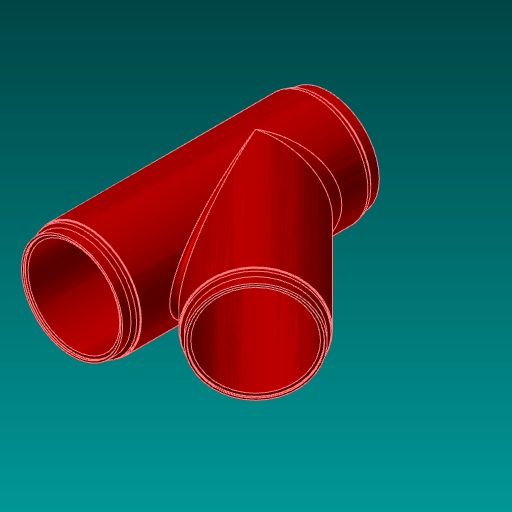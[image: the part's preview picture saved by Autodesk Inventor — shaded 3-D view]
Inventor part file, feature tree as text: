
AUTODESK INVENTOR PART (.ipt)
format: ipt  version: 2017.3 (Build 213256000, 256)  size: 343,040 bytes
history: native  units: in
note: dims shown in document units (in); Inventor stores cm internally (conversion verified against a paired STEP export)
features: extrude x12, sketch x8, fillet x6, chamfer x2, plane x1
ambient origin geometry x8: Origin, YZ Plane, XZ Plane, XY Plane, X Axis, Y Axis, Z Axis, Center Point
bodies: Solid1 (feature_tree)
feature tree (29):
  sketch  "Sketch1"  dims[d0=24.5in d1=27.0in]
  extrude  "Extrusion1"  Depth=27.0in
  plane  "Work Plane1"
  sketch  "Sketch2"  dims[d2=29.0in d3=49.0236in d4=19.4961in d5=0.0in d6=0.0in]
  extrude  "Extrusion2"  Depth=49.0236in TaperAngle=0.0deg
  extrude  "Extrusion3"  Depth=24.5in
  extrude  "Extrusion4"  Depth=29.0in
  extrude  "Extrusion5"  Depth=49.0236in
  extrude  "Extrusion6"  Depth=0.5in
  extrude  "Extrusion7"  TaperAngle=0.0deg  [1 undecoded]
  extrude  "Extrusion8"  Depth=0.5in
  extrude  "Extrusion9"  TaperAngle=0.0deg  [1 undecoded]
  fillet  "Fillet1"  Radius=46.0236in
  fillet  "Fillet2"  Radius=16.4961in
  fillet  "Fillet3"  [1 undecoded]
  fillet  "Fillet4"  Radius=46.0236in
  extrude  "Extrusion10"  TaperAngle=0.0deg  [1 undecoded]
  extrude  "Extrusion11"  Depth=49.0236in
  extrude  "Extrusion12"  TaperAngle=0.0deg  [1 undecoded]
  fillet  "Fillet5"  Radius=49.0236in
  chamfer  "Chamfer2"  [1 undecoded]
  fillet  "Fillet6"  Radius=1.0in
  chamfer  "Chamfer3"  Distance=6.0in
  sketch  "Sketch3"  dims[d7=45.0deg d8=24.5in]
  sketch  "Sketch4"  dims[d9=27.0in d10=29.0in]
  sketch  "Sketch5"  dims[d11=49.0236in d12=0.0in d13=26.0in]
  sketch  "Sketch6"  dims[d14=0.5in d15=0.0in d16=26.0in]
  sketch  "Sketch7"  dims[d17=0.5in d18=0.0in]
  sketch  "Sketch8"  dims[d19=26.0in d20=0.5in d21=0.0in d22=46.0236in d23=16.4961in d24=0.0in d25=0.0in d26=46.0236in d27=0.0in d28=49.0236in d29=0.0in d30=49.0236in d31=0.0in d32=1.0in d33=6.0in d34=1.0in d35=1.0in d39=28.48in d40=1.0in d41=0.0in d42=28.48in d43=1.0in d44=0.0in d45=28.48in d46=1.0in d47=0.0in d48=0.0312in d49=0.74in d50=0.125in d51=45.0deg d52=0.0312in d53=0.0312in d54=0.125in d55=45.0deg]
note: 6 required parameter values undecoded (feature->parameter linkage not recoverable at this tier; creation-order binding heuristic only, values carry confidence <= 0.55)
